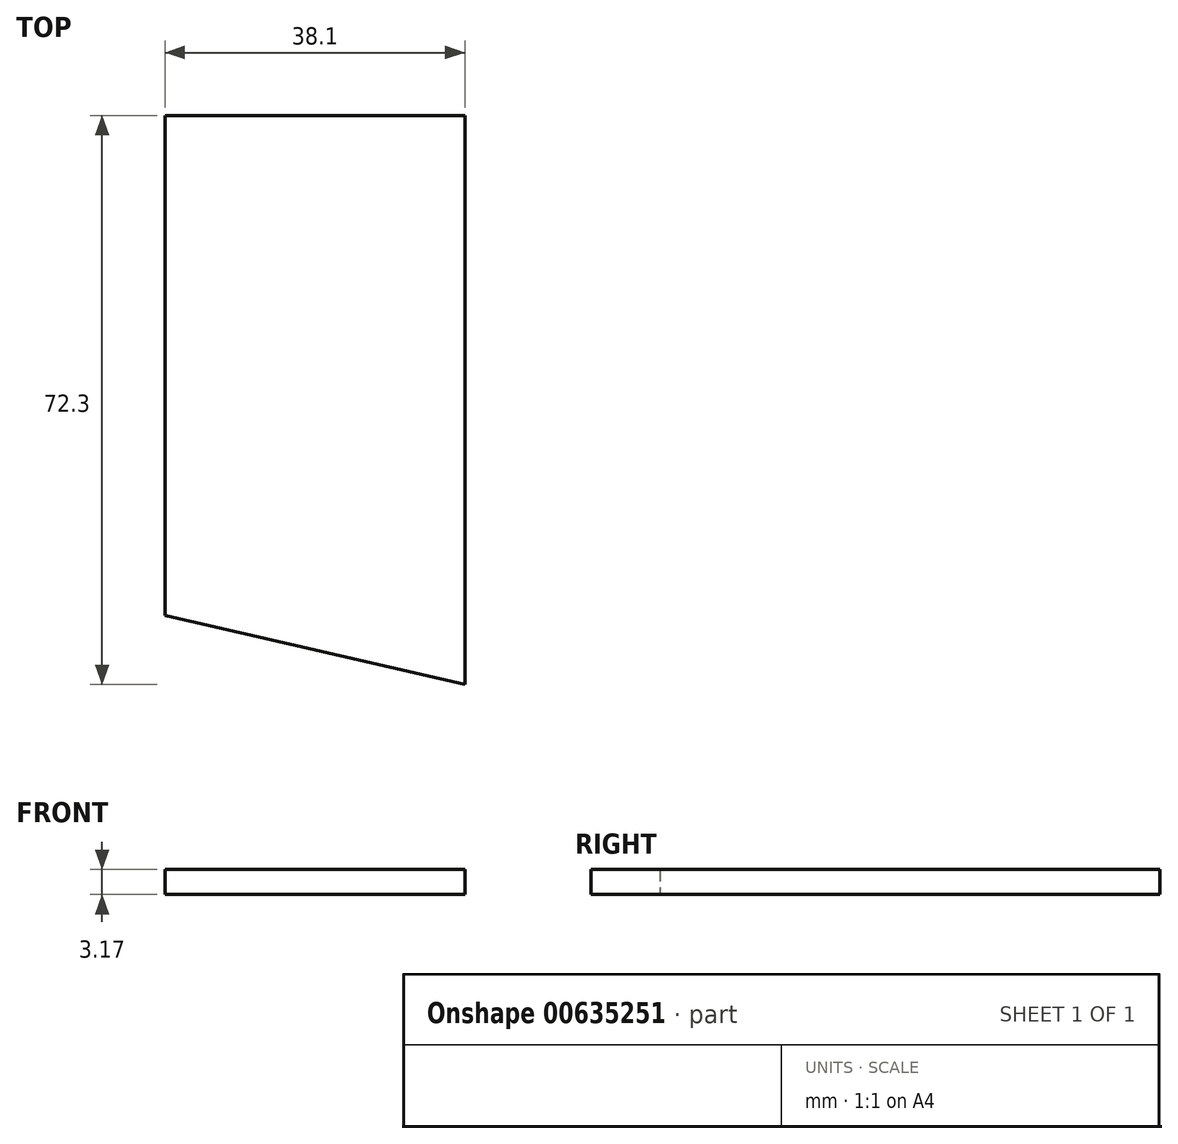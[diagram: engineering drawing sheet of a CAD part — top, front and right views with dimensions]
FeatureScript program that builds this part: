
annotation { "Feature Type Name" : "Feature", "Feature Type Description" : "" }
export const myFeature = defineFeature(function(context is Context, id is Id, definition is map)
    precondition{}
    {
        {
            var Q0;
            Q0=qCreatedBy(makeId("Top.planeOp"),FACE);
            var sketch = newSketch(context, id + "F0", { "sketchPlane" : qUnion([Q0])});
            skLineSegment(sketch, "E0.bottom", {"start": v(19.05, -31.75) * mm, "end": v(-19.05, -31.75) * mm});
            skLineSegment(sketch, "E0.top", {"start": v(19.05, 31.75) * mm, "end": v(-19.05, 31.75) * mm});
            skLineSegment(sketch, "E0.left", {"start": v(19.05, -31.75) * mm, "end": v(19.05, 31.75) * mm});
            skLineSegment(sketch, "E0.right", {"start": v(-19.05, -31.75) * mm, "end": v(-19.05, 31.75) * mm});
            skPoint(sketch, "E0.middle", {"position": v(0, 0) * mm});
            skLineSegment(sketch, "E1", {"start": v(-19.05, -31.75) * mm, "end": v(19.05, -40.55) * mm});
            skLineSegment(sketch, "E2", {"start": v(19.05, -40.55) * mm, "end": v(19.05, -31.75) * mm});
            skSolve(sketch);
        }
        {
            var Q0;
            Q0 = qSketchRegion(id + "F0", true);
            extrude(context, id + "F1", {"entities" : qUnion([Q0]), "depth" : 3.17 * mm, "offsetDistance" : 25.4 * mm});
        }
    });
